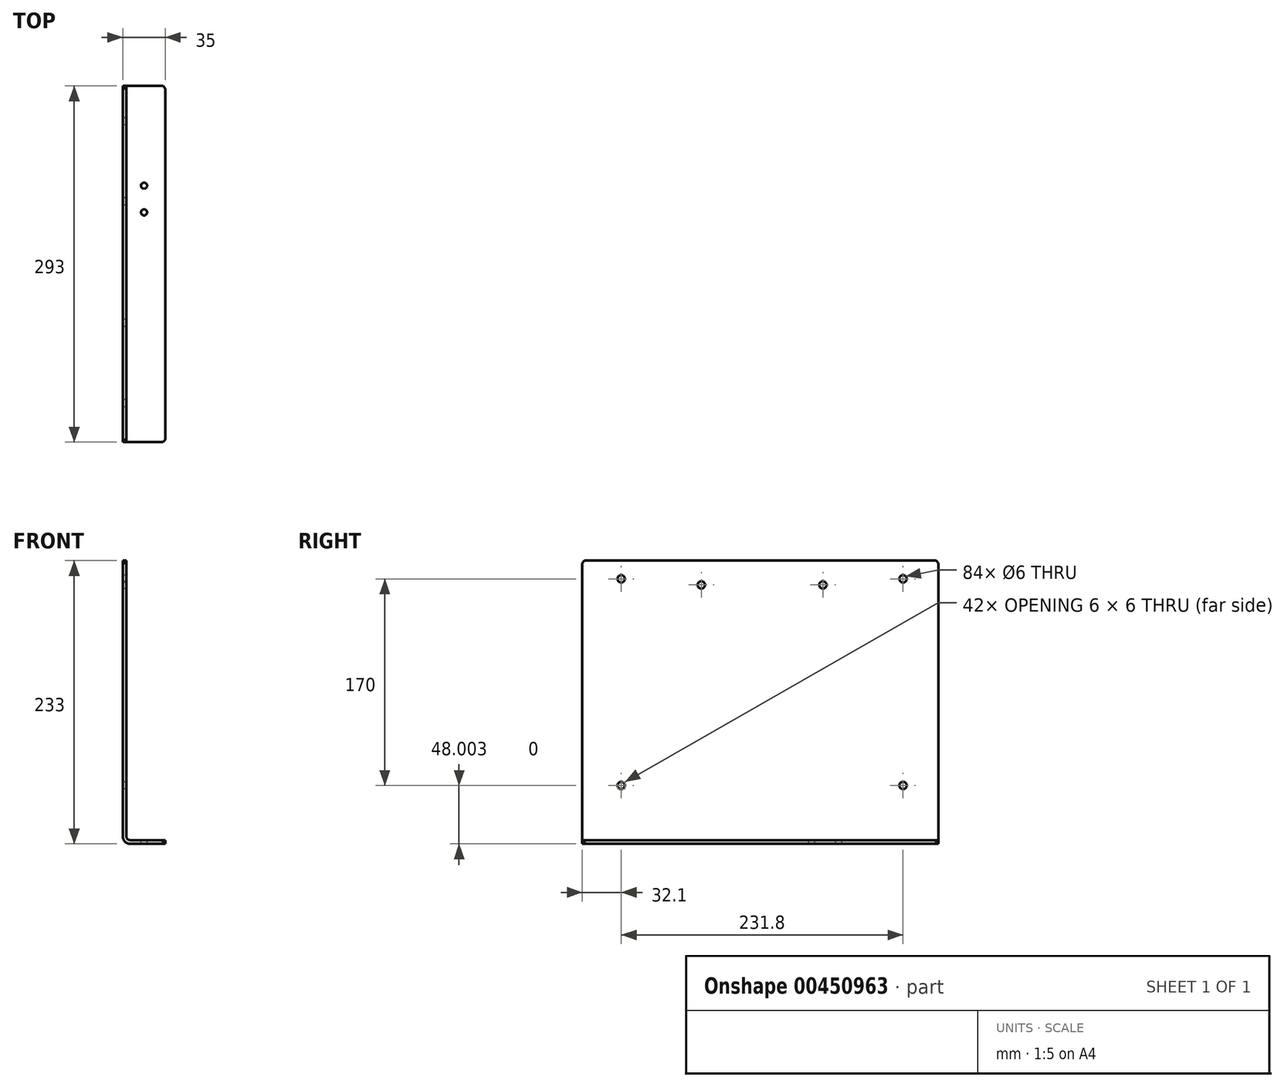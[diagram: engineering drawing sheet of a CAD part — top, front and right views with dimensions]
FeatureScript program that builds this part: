
annotation { "Feature Type Name" : "Feature", "Feature Type Description" : "" }
export const myFeature = defineFeature(function(context is Context, id is Id, definition is map)
    precondition{}
    {
        {
            var Q0;
            Q0=qCreatedBy(makeId("Front.planeOp"),FACE);
            var sketch = newSketch(context, id + "F0", { "sketchPlane" : qUnion([Q0])});
            skLineSegment(sketch, "E0", {"start": v(0.49, 209.68) * mm, "end": v(-295.51, 209.68) * mm});
            skLineSegment(sketch, "E1", {"start": v(0.49, 206.68) * mm, "end": v(-295.51, 206.68) * mm});
            skLineSegment(sketch, "E2", {"start": v(-295.51, 206.68) * mm, "end": v(-295.51, 239.68) * mm});
            skLineSegment(sketch, "E3", {"start": v(0.49, 206.68) * mm, "end": v(0.49, 239.68) * mm});
            skLineSegment(sketch, "E4", {"start": v(-1.51, 241.68) * mm, "end": v(0.49, 239.68) * mm});
            skLineSegment(sketch, "E5", {"start": v(0.49, -162.22) * mm, "end": v(0.49, 68.78) * mm});
            skLineSegment(sketch, "E6", {"start": v(-1.51, 70.78) * mm, "end": v(-293.51, 70.78) * mm});
            skLineSegment(sketch, "E7", {"start": v(0.49, -162.22) * mm, "end": v(-295.51, -162.22) * mm});
            skLineSegment(sketch, "E8", {"start": v(0.49, -159.22) * mm, "end": v(-295.51, -159.22) * mm});
            skLineSegment(sketch, "E9", {"start": v(-295.51, 68.78) * mm, "end": v(-295.51, -162.22) * mm});
            skLineSegment(sketch, "E10", {"start": v(122.29, 70.78) * mm, "end": v(119.29, 70.78) * mm});
            skLineSegment(sketch, "E11", {"start": v(119.29, -156.22) * mm, "end": v(119.29, 70.78) * mm});
            skArc(sketch, "E12", {"start": v(119.29, -156.22) * mm, "mid": v(121.05, -160.46) * mm, "end": v(125.29, -162.22) * mm});
            skLineSegment(sketch, "E13", {"start": v(122.29, -156.22) * mm, "end": v(122.29, 70.78) * mm});
            skArc(sketch, "E14", {"start": v(122.29, -156.22) * mm, "mid": v(123.17, -158.34) * mm, "end": v(125.29, -159.22) * mm});
            skLineSegment(sketch, "E15", {"start": v(125.29, -159.22) * mm, "end": v(154.29, -159.22) * mm});
            skLineSegment(sketch, "E16", {"start": v(125.29, -162.22) * mm, "end": v(154.29, -162.22) * mm});
            skLineSegment(sketch, "E17", {"start": v(154.29, -159.22) * mm, "end": v(154.29, -162.22) * mm});
            skLineSegment(sketch, "E18", {"start": v(-1.51, 241.68) * mm, "end": v(-293.51, 241.68) * mm});
            skLineSegment(sketch, "E19", {"start": v(-295.51, 239.68) * mm, "end": v(-293.51, 241.68) * mm});
            skCircle(sketch, "E20", {"center": v(-197.51, 50.78) * mm, "radius": 3 * mm});
            skLineSegment(sketch, "E21", {"start": v(-193.61, 50.78) * mm, "end": v(-201.41, 50.78) * mm});
            skLineSegment(sketch, "E22", {"start": v(-197.51, 54.68) * mm, "end": v(-197.51, 46.88) * mm});
            skCircle(sketch, "E23", {"center": v(-97.51, 50.78) * mm, "radius": 3 * mm});
            skLineSegment(sketch, "E24", {"start": v(-93.61, 50.78) * mm, "end": v(-101.41, 50.78) * mm});
            skLineSegment(sketch, "E25", {"start": v(-97.51, 54.68) * mm, "end": v(-97.51, 46.88) * mm});
            skLineSegment(sketch, "E26", {"start": v(-211.01, 223.43) * mm, "end": v(-211.01, 230.93) * mm});
            skCircle(sketch, "E27", {"center": v(-211.01, 227.18) * mm, "radius": 2.07 * mm});
            skCircle(sketch, "E28", {"center": v(-211.01, 227.18) * mm, "radius": 2.5 * mm});
            skLineSegment(sketch, "E29", {"start": v(-214.76, 227.18) * mm, "end": v(-207.26, 227.18) * mm});
            skLineSegment(sketch, "E30", {"start": v(-189.01, 223.43) * mm, "end": v(-189.01, 230.93) * mm});
            skCircle(sketch, "E31", {"center": v(-189.01, 227.18) * mm, "radius": 2.07 * mm});
            skCircle(sketch, "E32", {"center": v(-189.01, 227.18) * mm, "radius": 2.5 * mm});
            skLineSegment(sketch, "E33", {"start": v(-192.76, 227.18) * mm, "end": v(-185.26, 227.18) * mm});
            skLineSegment(sketch, "E34", {"start": v(0.49, 68.78) * mm, "end": v(-1.51, 70.78) * mm});
            skLineSegment(sketch, "E35", {"start": v(-293.51, 70.78) * mm, "end": v(-295.51, 68.78) * mm});
            skCircle(sketch, "E36", {"center": v(-31.61, 55.78) * mm, "radius": 3 * mm});
            skLineSegment(sketch, "E37", {"start": v(-35.51, 55.78) * mm, "end": v(-27.71, 55.78) * mm});
            skLineSegment(sketch, "E38", {"start": v(-31.61, 51.88) * mm, "end": v(-31.61, 59.68) * mm});
            skCircle(sketch, "E39", {"center": v(-31.61, -114.22) * mm, "radius": 3 * mm});
            skLineSegment(sketch, "E40", {"start": v(-35.51, -114.22) * mm, "end": v(-27.71, -114.22) * mm});
            skLineSegment(sketch, "E41", {"start": v(-31.61, -118.12) * mm, "end": v(-31.61, -110.32) * mm});
            skCircle(sketch, "E42", {"center": v(-263.41, -114.22) * mm, "radius": 3 * mm});
            skLineSegment(sketch, "E43", {"start": v(-267.31, -114.22) * mm, "end": v(-259.51, -114.22) * mm});
            skLineSegment(sketch, "E44", {"start": v(-263.41, -118.12) * mm, "end": v(-263.41, -110.32) * mm});
            skCircle(sketch, "E45", {"center": v(-263.41, 55.78) * mm, "radius": 3 * mm});
            skLineSegment(sketch, "E46", {"start": v(-267.31, 55.78) * mm, "end": v(-259.51, 55.78) * mm});
            skLineSegment(sketch, "E47", {"start": v(-263.41, 51.88) * mm, "end": v(-263.41, 59.68) * mm});
            skLineSegment(sketch, "E48", {"start": v(-32.5, 120.46) * mm, "end": v(-22.9, 120.46) * mm});
            skLineSegment(sketch, "E49", {"start": v(-32.5, 120.46) * mm, "end": v(-27.7, 128.46) * mm});
            skLineSegment(sketch, "E50", {"start": v(-27.7, 128.46) * mm, "end": v(-22.9, 120.46) * mm});
            skLineSegment(sketch, "E51", {"start": v(-66.11, 105.76) * mm, "end": v(-56.51, 105.76) * mm});
            skLineSegment(sketch, "E52", {"start": v(-66.11, 105.76) * mm, "end": v(-61.31, 113.76) * mm});
            skLineSegment(sketch, "E53", {"start": v(-61.31, 113.76) * mm, "end": v(-56.51, 105.76) * mm});
            skLineSegment(sketch, "E54", {"start": v(-167.74, 120.15) * mm, "end": v(-158.14, 120.15) * mm});
            skLineSegment(sketch, "E55", {"start": v(-167.74, 120.15) * mm, "end": v(-162.94, 128.15) * mm});
            skLineSegment(sketch, "E56", {"start": v(-162.94, 128.15) * mm, "end": v(-158.14, 120.15) * mm});
            skLineSegment(sketch, "E57", {"start": v(-164.45, 134.66) * mm, "end": v(-154.85, 134.66) * mm});
            skLineSegment(sketch, "E58", {"start": v(-164.45, 134.66) * mm, "end": v(-159.65, 142.66) * mm});
            skLineSegment(sketch, "E59", {"start": v(-159.65, 142.66) * mm, "end": v(-154.85, 134.66) * mm});
            skLineSegment(sketch, "E60", {"start": v(-110.46, 171.62) * mm, "end": v(-100.86, 171.62) * mm});
            skLineSegment(sketch, "E61", {"start": v(-110.46, 171.62) * mm, "end": v(-105.66, 179.62) * mm});
            skLineSegment(sketch, "E62", {"start": v(-105.66, 179.62) * mm, "end": v(-100.86, 171.62) * mm});
            skSolve(sketch);
        }
        {
            var Q0;
            Q0=makeQuery(id+"F0.imprint","IMPRINT",FACE,{"disambiguationData":[TD([[makeQuery(id+"F0.imprint","IMPRINT",EDGE,{"derivedFrom":sQuery(id+"F0.wireOp",EDGE,"E10")}),1.0]])]});
            extrude(context, id + "F1", {"entities" : qUnion([Q0]), "oppositeDirection" : true, "depth" : 293 * mm});
        }
        {
            var Q0;
            Q0=makeQuery(id+"F1.opExtrude","SWEPT_FACE",FACE,{"disambiguationData":[OSD([sQuery(id+"F0.wireOp",EDGE,"E15")])]});
            var sketch = newSketch(context, id + "F2", { "sketchPlane" : qUnion([Q0])});
            skLineSegment(sketch, "E63.0", {"start": v(125.29, 189) * mm, "end": v(154.29, 189) * mm});
            skLineSegment(sketch, "E64.0", {"start": v(125.29, 211) * mm, "end": v(154.29, 211) * mm});
            skLineSegment(sketch, "E65.0", {"start": v(136.79, 293) * mm, "end": v(136.79, 0) * mm});
            skPoint(sketch, "E66", {"position": v(136.79, 189) * mm});
            skPoint(sketch, "E67", {"position": v(136.79, 211) * mm});
            skSolve(sketch);
        }
        {
            var Q0;
            Q0=sQuery(id+"F2.wireOp",VERTEX,"E66");
            var Q1;
            Q1=sQuery(id+"F2.wireOp",VERTEX,"E67");
            var Q2;
            Q2=makeQuery(id+"F1.opExtrude","SWEPT_BODY",BODY,{"disambiguationData":[OSD([sQuery(id+"F0.wireOp",EDGE,"E10"),sQuery(id+"F0.wireOp",EDGE,"E11"),sQuery(id+"F0.wireOp",EDGE,"E12"),sQuery(id+"F0.wireOp",EDGE,"E13"),sQuery(id+"F0.wireOp",EDGE,"E14"),sQuery(id+"F0.wireOp",EDGE,"E15"),sQuery(id+"F0.wireOp",EDGE,"E16"),sQuery(id+"F0.wireOp",EDGE,"E17")])]});
            hole(context, id + "F3", {"style" : HoleStyle.SIMPLE, "endStyle" : HoleEndStyle.THROUGH, "holeDiameter" : 5 * mm, "isTappedThrough" : true, "tappedDepth" : 12 * mm, "tapClearance" : 3, "locations" : qUnion([Q0, Q1]), "scope" : qUnion([Q2])});
        }
        {
            var Q0;
            Q0=makeQuery(id+"F1.opExtrude","SWEPT_FACE",FACE,{"disambiguationData":[OSD([sQuery(id+"F0.wireOp",EDGE,"E11")])]});
            var sketch = newSketch(context, id + "F4", { "sketchPlane" : qUnion([Q0])});
            skPoint(sketch, "E68", {"position": v(-32.1, 55.78) * mm});
            skPoint(sketch, "E69", {"position": v(-32.1, -114.22) * mm});
            skPoint(sketch, "E70.MirrorP", {"position": v(-263.9, 55.78) * mm});
            skPoint(sketch, "E71.MirrorP", {"position": v(-263.9, -114.22) * mm});
            skPoint(sketch, "E72", {"position": v(-98, 50.78) * mm});
            skPoint(sketch, "E73.MirrorP", {"position": v(-198, 50.78) * mm});
            skSolve(sketch);
        }
        {
            var Q0;
            Q0=sQuery(id+"F4.wireOp",VERTEX,"E68");
            var Q1;
            Q1=sQuery(id+"F4.wireOp",VERTEX,"E69");
            var Q2;
            Q2=sQuery(id+"F4.wireOp",VERTEX,"E71.MirrorP");
            var Q3;
            Q3=sQuery(id+"F4.wireOp",VERTEX,"E70.MirrorP");
            var Q4;
            Q4=sQuery(id+"F4.wireOp",VERTEX,"E72");
            var Q5;
            Q5=sQuery(id+"F4.wireOp",VERTEX,"E73.MirrorP");
            var Q6;
            Q6=makeQuery(id+"F1.opExtrude","SWEPT_BODY",BODY,{"disambiguationData":[OSD([sQuery(id+"F0.wireOp",EDGE,"E10"),sQuery(id+"F0.wireOp",EDGE,"E11"),sQuery(id+"F0.wireOp",EDGE,"E12"),sQuery(id+"F0.wireOp",EDGE,"E13"),sQuery(id+"F0.wireOp",EDGE,"E14"),sQuery(id+"F0.wireOp",EDGE,"E15"),sQuery(id+"F0.wireOp",EDGE,"E16"),sQuery(id+"F0.wireOp",EDGE,"E17")])]});
            hole(context, id + "F5", {"style" : HoleStyle.SIMPLE, "endStyle" : HoleEndStyle.THROUGH, "holeDiameter" : 6 * mm, "isTappedThrough" : true, "tappedDepth" : 12 * mm, "tapClearance" : 3, "locations" : qUnion([Q0, Q1, Q2, Q3, Q4, Q5]), "scope" : qUnion([Q6])});
        }
        {
            var Q0;
            Q0=makeQuery(id+"F1.opExtrude","CAP_EDGE",EDGE,{"disambiguationData":[OSD([sQuery(id+"F0.wireOp",EDGE,"E10")])],"isStart":true});
            var Q1;
            Q1=makeQuery(id+"F1.opExtrude","CAP_EDGE",EDGE,{"disambiguationData":[OSD([sQuery(id+"F0.wireOp",EDGE,"E10")])],"isStart":false});
            var Q2;
            Q2=makeQuery(id+"F1.opExtrude","CAP_EDGE",EDGE,{"disambiguationData":[OSD([sQuery(id+"F0.wireOp",EDGE,"E17")])],"isStart":false});
            chamfer(context, id + "F6", {"entities" : qUnion([Q0, Q1, Q2]), "width" : 2 * mm, "tangentPropagation" : true});
        }
        {
            var Q0;
            Q0=makeQuery(id+"F1.opExtrude","CAP_EDGE",EDGE,{"disambiguationData":[OSD([sQuery(id+"F0.wireOp",EDGE,"E17")])],"isStart":true});
            chamfer(context, id + "F7", {"entities" : qUnion([Q0]), "width" : 2 * mm, "tangentPropagation" : true});
        }
    });
